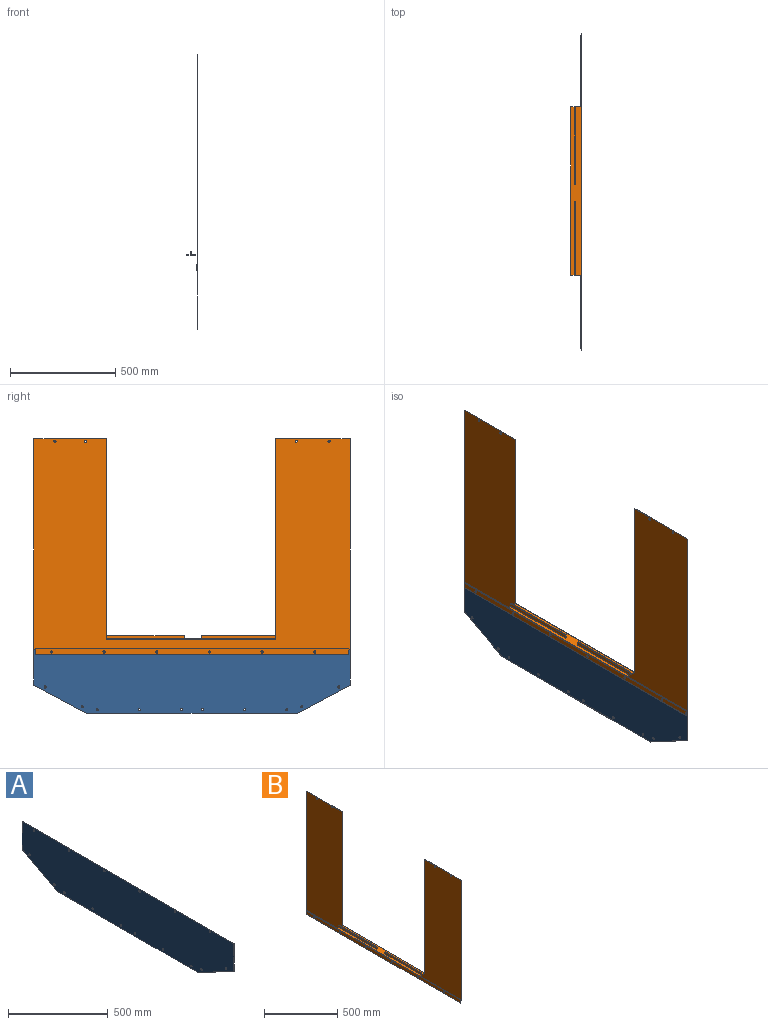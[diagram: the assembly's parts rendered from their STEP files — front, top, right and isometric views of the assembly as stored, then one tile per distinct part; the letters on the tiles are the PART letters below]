
ASSEMBLY  parts=2 mates=1
PART A: 24 faces, bbox 2x1501x304 mm
  f0: plane 1501x2mm, normal (0,0,1), area 3002mm2, adj f3,f5,f12,f13
  f1: plane 251.79x134.3mm, normal (0,-0.47,-0.88), area 570.7mm2, adj f2,f3,f12,f13
  f2: plane 997.42x2mm, normal (0,0,-1), area 1994.8mm2, adj f1,f4,f12,f13
  f3: plane 169.7x2mm, normal (0,-1,0), area 339.4mm2, adj f0,f1,f12,f13
  f4: plane 251.79x134.3mm, normal (0,0.47,-0.88), area 570.7mm2, adj f2,f5,f12,f13
  f5: plane 169.7x2mm, normal (0,1,0), area 339.4mm2, adj f0,f4,f12,f13
  f6: cylinder r=5mm len=10mm, axis (1,0,0), area 62.8mm2, adj f12,f13
  f7: cylinder r=5mm len=10mm, axis (1,0,0), area 62.8mm2, adj f12,f13
  f8: cylinder r=5mm len=10mm, axis (1,0,0), area 62.8mm2, adj f12,f13
  f9: cylinder r=5mm len=10mm, axis (1,0,0), area 62.8mm2, adj f12,f13
  f10: cylinder r=5mm len=10mm, axis (1,0,0), area 62.8mm2, adj f12,f13
  f11: cylinder r=5mm len=10mm, axis (1,0,0), area 62.8mm2, adj f12,f13
  f12: plane 1501x304mm, normal (-1,0,0), area 421232mm2, adj f0,f1,f2,f3,f4,f5,f6,f7
  f13: plane 1501x304mm, normal (1,0,0), area 421232mm2, adj f0,f1,f2,f3,f4,f5,f6,f7
  f14: cylinder r=5mm len=10mm, axis (1,0,0), area 62.8mm2, adj f12,f13
  f15: cylinder r=5mm len=10mm, axis (1,0,0), area 62.8mm2, adj f12,f13
  f16: cylinder r=5mm len=10mm, axis (1,0,0), area 62.8mm2, adj f12,f13
  f17: cylinder r=5mm len=10mm, axis (1,0,0), area 62.8mm2, adj f12,f13
  f18: cylinder r=5mm len=10mm, axis (1,0,0), area 62.8mm2, adj f12,f13
  f19: cylinder r=5mm len=10mm, axis (1,0,0), area 62.8mm2, adj f12,f13
  f20: cylinder r=5mm len=10mm, axis (1,0,0), area 62.8mm2, adj f12,f13
  f21: cylinder r=5mm len=10mm, axis (1,0,0), area 62.8mm2, adj f12,f13
  f22: cylinder r=5mm len=10mm, axis (1,0,0), area 62.8mm2, adj f12,f13
  f23: cylinder r=5mm len=10mm, axis (1,0,0), area 62.8mm2, adj f12,f13
PART B: 40 faces, bbox 52x1501x1025.5 mm
  f0: plane 352x5mm, normal (0,0,1), area 1760mm2, adj f1,f2,f3,f4
  f1: plane 50x17mm, normal (0,-1,0), area 175mm2, adj f0,f2,f4,f5,f6,f7,f8,f30
  f2: plane 352x15mm, normal (1,0,0), area 5280mm2, adj f0,f1,f3,f6
  f3: plane 15x5mm, normal (0,1,0), area 75mm2, adj f0,f2,f4,f6
  f4: plane 352x15mm, normal (-1,0,0), area 5280mm2, adj f0,f1,f3,f6
  f5: plane 352x5mm, normal (0,0,-1), area 1760mm2, adj f1,f7
  f6: plane 800x52mm, normal (0,0,1), area 38000mm2, adj f1,f2,f3,f4,f8,f9,f10,f11
  f7: plane 800x50mm, normal (0,0,-1), area 36400mm2, adj f1,f5,f8,f11,f15,f30
  f8: plane 800x2mm, normal (-1,0,0), area 1600mm2, adj f1,f6,f7,f11
  f9: plane 950.5x2mm, normal (0,1,0), area 1901mm2, adj f6,f16,f23,f30
  f10: plane 950.5x2mm, normal (0,-1,0), area 1901mm2, adj f6,f23,f30,f31
  f11: plane 50x17mm, normal (0,1,0), area 175mm2, adj f6,f7,f8,f12,f14,f15,f21,f30
  f12: plane 368x15mm, normal (1,0,0), area 5520mm2, adj f6,f11,f13,f21
  f13: plane 15x5mm, normal (0,-1,0), area 75mm2, adj f6,f12,f14,f21
  f14: plane 368x15mm, normal (-1,0,0), area 5520mm2, adj f6,f11,f13,f21
  f15: plane 368x5mm, normal (0,0,-1), area 1840mm2, adj f7,f11
  f16: plane 355.5x2mm, normal (0,0,1), area 711mm2, adj f9,f23,f24,f30
  f17: cylinder r=5mm len=10mm, axis (1,0,0), area 62.8mm2, adj f23,f30
  f18: cylinder r=5mm len=10mm, axis (1,0,0), area 62.8mm2, adj f23,f30
  f19: cylinder r=5mm len=10mm, axis (1,0,0), area 62.8mm2, adj f23,f30
  f20: cylinder r=5mm len=10mm, axis (1,0,0), area 62.8mm2, adj f23,f30
  f21: plane 368x5mm, normal (0,0,1), area 1840mm2, adj f11,f12,f13,f14
  f22: plane 27x5mm, normal (0,-1,0), area 60mm2, adj f25,f27,f28,f30,f32,f33
  f23: plane 1501x1000.5mm, normal (1,0,0), area 741036.3mm2, adj f6,f9,f10,f16,f17,f18,f19,f20
  f24: plane 1000.5x2mm, normal (0,-1,0), area 2001mm2, adj f16,f23,f25,f30
  f25: plane 1501x5mm, normal (0,0,-1), area 7460mm2, adj f22,f23,f24,f26,f29,f30,f33
  f26: plane 1000.5x2mm, normal (0,1,0), area 2001mm2, adj f23,f25,f30,f31
  f27: plane 1486x5mm, normal (0,0,1), area 7430mm2, adj f22,f29,f30,f32
  f28: plane 1486x2mm, normal (0,0,-1), area 2972mm2, adj f22,f29,f32,f33
  f29: plane 27x5mm, normal (0,1,0), area 60mm2, adj f25,f27,f28,f30,f32,f33
  f30: plane 1501x1000.5mm, normal (-1,0,0), area 736464.3mm2, adj f1,f7,f9,f10,f11,f16,f17,f18
  f31: plane 345.5x2mm, normal (0,0,1), area 691mm2, adj f10,f23,f26,f30
  f32: plane 1486x27mm, normal (-1,0,0), area 39650.8mm2, adj f22,f27,f28,f29,f34,f35,f36,f37
  f33: plane 1486x25mm, normal (1,0,0), area 36678.8mm2, adj f22,f25,f28,f29,f34,f35,f36,f37
  f34: cylinder r=5mm len=10mm, axis (1,0,0), area 62.8mm2, adj f32,f33
  f35: cylinder r=5mm len=10mm, axis (1,0,0), area 62.8mm2, adj f32,f33
  f36: cylinder r=5mm len=10mm, axis (1,0,0), area 62.8mm2, adj f32,f33
  f37: cylinder r=5mm len=10mm, axis (1,0,0), area 62.8mm2, adj f32,f33
  f38: cylinder r=5mm len=10mm, axis (1,0,0), area 62.8mm2, adj f32,f33
  f39: cylinder r=5mm len=10mm, axis (1,0,0), area 62.8mm2, adj f32,f33
PLACE A t=(-123.33,-827.44,524.67)mm
PLACE B t=(-123.33,-827.44,524.67)mm fixed
MATE fastened A.f10 <-> B.f36  axis (-1,0,0) through (-125.33,-659.44,-486.33)mm
